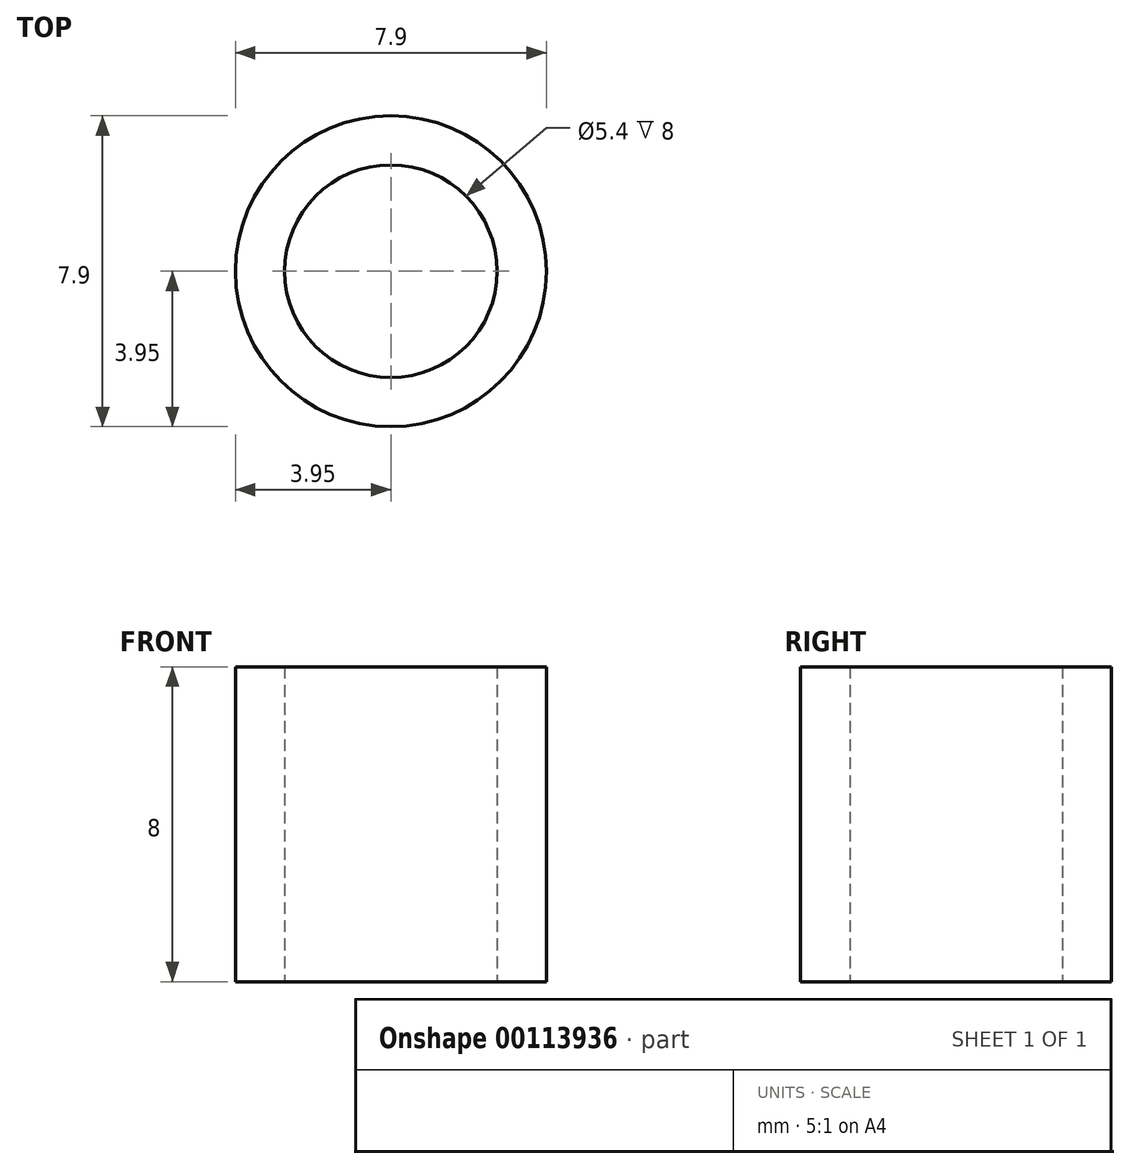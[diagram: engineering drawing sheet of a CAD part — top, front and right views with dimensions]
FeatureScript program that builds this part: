
annotation { "Feature Type Name" : "Feature", "Feature Type Description" : "" }
export const myFeature = defineFeature(function(context is Context, id is Id, definition is map)
    precondition{}
    {
        {
            var Q0;
            Q0=qCreatedBy(makeId("Top.planeOp"),FACE);
            var sketch = newSketch(context, id + "F0", { "sketchPlane" : qUnion([Q0])});
            skCircle(sketch, "E0", {"center": v(0, 0) * mm, "radius": 3.95 * mm});
            skCircle(sketch, "E1", {"center": v(0, 0) * mm, "radius": 2.7 * mm});
            skSolve(sketch);
        }
        {
            var Q0;
            Q0=makeQuery(id+"F0.imprint","IMPRINT",FACE,{"disambiguationData":[TD([[makeQuery(id+"F0.imprint","IMPRINT",EDGE,{"derivedFrom":sQuery(id+"F0.wireOp",EDGE,"E0")}),1.0]])]});
            extrude(context, id + "F1", {"entities" : qUnion([Q0]), "depth" : 8 * mm});
        }
    });
